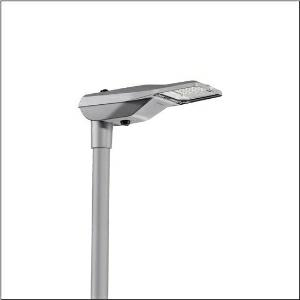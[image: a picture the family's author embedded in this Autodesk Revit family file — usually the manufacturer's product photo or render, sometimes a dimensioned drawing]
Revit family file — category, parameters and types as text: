
# Revit family: streetlight_sl_21_iq_micro___st1_0a_5xe1d51y08db_19c1
name_source: partatom
category: Lighting Fixtures
units: mm (PartAtom-declared; Revit-internal decimal feet)

## family parameters
Cut with Voids When Loaded = No
Host = Face
Light Source = No
Part Type = Normal
Room Calculation Point = No
Round Connector Dimension = Use Diameter
Shared = No

## types (1)
- --- (1 x LED, 4490 lm, 39.1 W, 3000K)
    Apparent Load = 39 VA
    CIE Flux Codes = 37 72 97 100 100
    Color Rendering = 80
    Color Temperature = 3000K
    Default Elevation = 1800 mm
    Description = Streetlight SL 21 iQ micro, mast luminaire, primary light control with lens, of PMMA, primary optical cover: cover, of toughened safety glass, transparent, light distribution: ST1.0a, light emission: direct distribution, primary light characteristic: asymmetric, installation type: post-top, side-entry, LED, High Power LED, rated luminous flux: 4.490lm, luminous efficacy: 115lm/W, light colour: 830, colour temperature: 3000K, control gear: iQ-Street Remote, D4i with power reduction, control: pre-setting: logarithmic dimming characteristic, Street-Remote, Auto-Match, Temp-Guard, Lumen-Switch, Night-Set, Smart-Wire, Light-Fading, Desk-Remote (wireless, voltage-free reading and setting of iQ features in the workshop via application-optimized NFC function/RFID function), optimised constant luminous flux control (CLO 2.0), mains connection: 220..240V, AC, 50/60Hz, start of lifetime: 39W, end of service life: 41W, reduction: 17W, luminaire housing, of diecast aluminium, powder-coated, SITECO metallic grey (DB 702S), corrosivity category C5 high according to DIN EN ISO 12944, please order mast flange separately, inclination adjustable: 0°, 5°, 10°, 15°, sealing non-destructively replaceable, multi-level sealing system, length: 528mm, width: 235mm, height: 110mm, mast flange for spigot size: 42mm (side-entry): 5XC10008XM4, 60/48mm (side-entry/post-top): 5XC10108XM2, 76/60mm (side-entry/post-top): 5XC10108XM1, mounting height: 4..8m, Smart Interface below and above, protection rating (complete): IP66, insulation class (complete): insulation class II (safety insulation), certification: CE, ENEC, ENEC+, VDE, impact resistance: IK10, permissible operating ambient temperature for outdoor applications: -40..+50°C, standard-compliant lighting for roads and squares, packaging unit: 1 piece

Light Distribution: ST1.0a
    Height = 110 mm
    Lamp = 1 x LED
    Lamp Light Flux = 4490 lm
    Lamp Power = 39.1 W
    Lamp count = 1
    Length = 528 mm
    Luminous efficacy = 115 lm/W
    Manufacturer = Siteco
    ModVariant = No
    Model = 5XE1D51Y08DB
    Number of Poles = 1
    OnlyDefault = Yes
    Power Factor = 1
    Product Name = Streetlight SL 21 iQ micro | ST1.0a
    Product group = mast luminaire | pylon top
    ProductGroupID = 6100
    Protection Class = Protection class II
    Protection Degree = IP 66
    RLX_Detail_Level = 1
    RLX_Emergency_Light_Flux = 0 lm
    RLX_Emergency_Type = 0
    RLX_Emergency_Type_DB = No
    RlxData = <blob elided: 98473 chars, md5=3bc6a73f>
    Socket = socket
    Standby Power = 0 W
    System Light Flux = 4490 lm
    System Power = 39 W
    Type Comments = factory setting: luminous flux: 100 % | dim-lin: 254 | 765 mA
    Type Image = l_1007239.jpg
    URL = http://relux.com
    VarID = @adj_115465
    Voltage = 0 V
    Weight = 0.00 kg
    Width = 235 mm

## geometry (parser evidence)
native form markers: Blend x4, Sweep x12
no freeform markers — native parametric forms only
